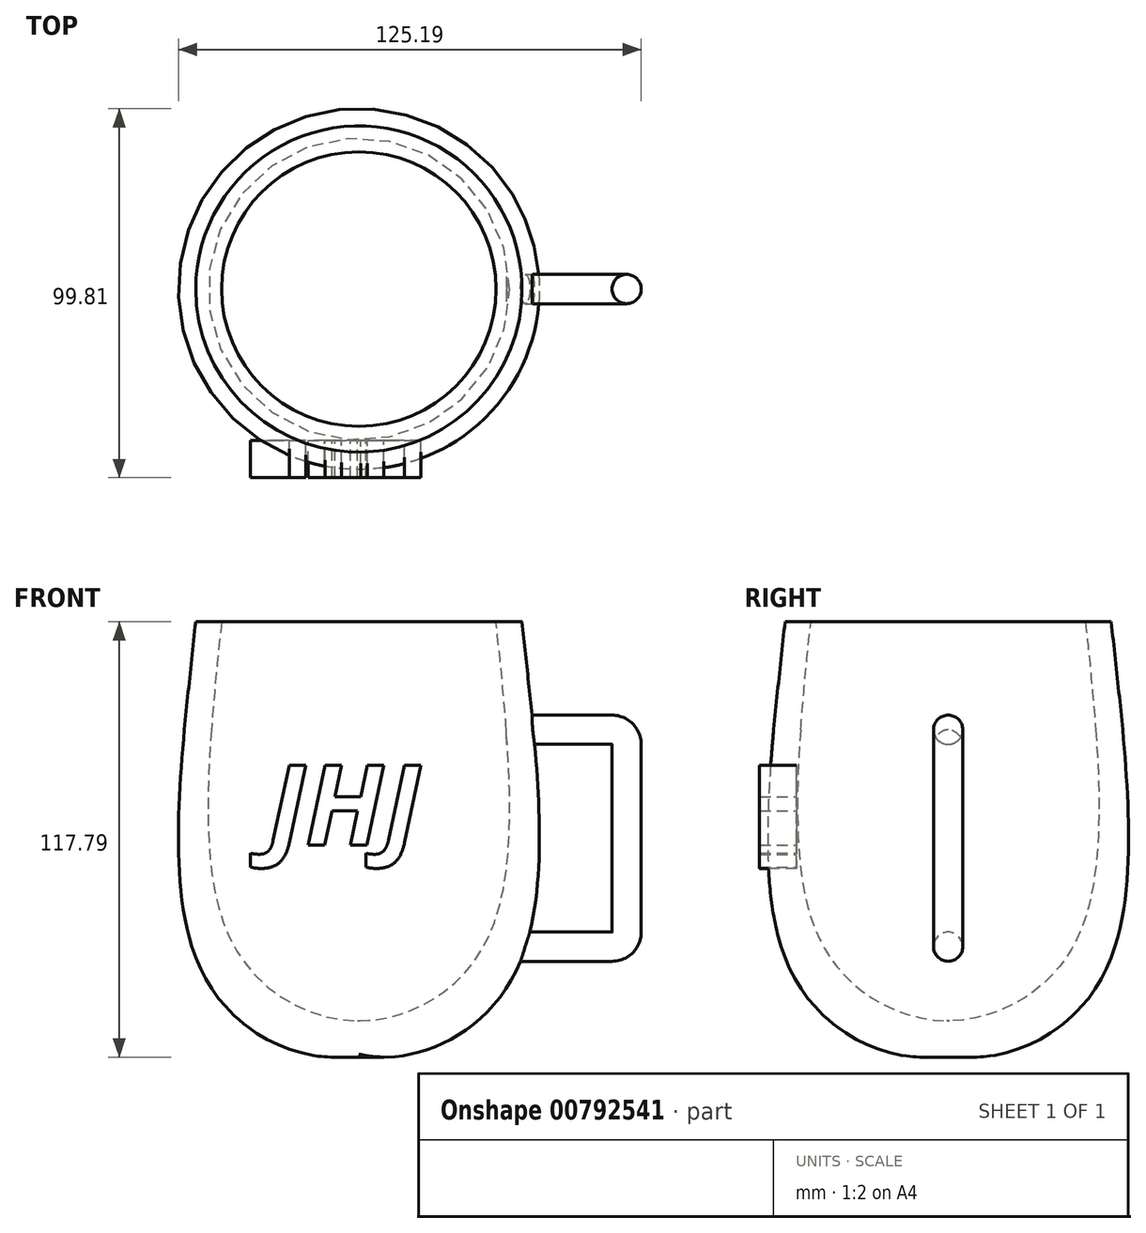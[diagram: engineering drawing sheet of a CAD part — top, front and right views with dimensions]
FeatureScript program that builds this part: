
annotation { "Feature Type Name" : "Feature", "Feature Type Description" : "" }
export const myFeature = defineFeature(function(context is Context, id is Id, definition is map)
    precondition{}
    {
        {
            var Q0;
            Q0=qCreatedBy(makeId("Front.planeOp"),FACE);
            var sketch = newSketch(context, id + "F0", { "sketchPlane" : qUnion([Q0])});
            skFitSpline(sketch, "E0", {"points": [v(0, -61.73) * mm, v(36.41, -35.88) * mm, v(35.16, 93.65) * mm], "startDerivative": vector(97.28, -1.16) * mm, "endDerivative": vector(18.9, 148.96) * mm});
            skFitSpline(sketch, "E1", {"points": [v(0, -70.74) * mm, v(43.6, -45.95) * mm, v(42.98, 94.18) * mm], "startDerivative": vector(109.3, -28.64) * mm, "endDerivative": vector(27.71, 172.05) * mm});
            skLineSegment(sketch, "E2", {"start": v(37.13, 46.22) * mm, "end": v(44.12, 46.22) * mm});
            skLineSegment(sketch, "E3", {"start": v(39.9, 16.99) * mm, "end": v(68.42, 16.99) * mm});
            skLineSegment(sketch, "E4", {"start": v(72.42, 12.99) * mm, "end": v(72.42, -37.71) * mm});
            skLineSegment(sketch, "E5", {"start": v(68.42, -41.71) * mm, "end": v(36.41, -41.71) * mm});
            skPoint(sketch, "E6.visualSharp", {"position": v(72.42, 16.99) * mm});
            skArc(sketch, "E6.filletArc", {"start": v(72.42, 12.99) * mm, "mid": v(71.25, 15.81) * mm, "end": v(68.42, 16.99) * mm});
            skPoint(sketch, "E7.visualSharp", {"position": v(72.42, -41.71) * mm});
            skArc(sketch, "E7.filletArc", {"start": v(68.42, -41.71) * mm, "mid": v(71.25, -40.54) * mm, "end": v(72.42, -37.71) * mm});
            skLineSegment(sketch, "E8", {"start": v(0, -70.74) * mm, "end": v(0, 56.7) * mm});
            skSolve(sketch);
        }
        {
            var Q0;
            {var subQ0=sQuery(id+"F0.wireOp",EDGE,"E2");Q0=makeQuery(id+"F0.imprint","IMPRINT",FACE,{"disambiguationData":[TD([[makeQuery(id+"F0.imprint","IMPRINT",EDGE,{"derivedFrom":subQ0}),-1.0]])]});}
            var Q1;
            {var subQ0=sQuery(id+"F0.wireOp",EDGE,"E5");var subQ1=sQuery(id+"F0.wireOp",EDGE,"E0");var subQ2=makeQuery(id+"F0.imprint","INTERSECT",VERTEX,{"derivedFrom":[subQ1,subQ0]});Q1=makeQuery(id+"F0.imprint","IMPRINT",FACE,{"disambiguationData":[TD([[makeQuery(id+"F0.imprint","IMPRINT",EDGE,{"disambiguationData":[TD([[subQ2,-1.0]])],"derivedFrom":subQ1}),-1.0]])]});}
            var Q2;
            {var subQ0=sQuery(id+"F0.wireOp",EDGE,"E8");var subQ1=sQuery(id+"F0.wireOp",EDGE,"E0");var subQ2=makeQuery(id+"F0.imprint","INTERSECT",VERTEX,{"derivedFrom":[subQ1,subQ0]});Q2=makeQuery(id+"F0.imprint","IMPRINT",FACE,{"disambiguationData":[TD([[makeQuery(id+"F0.imprint","IMPRINT",EDGE,{"disambiguationData":[TD([[subQ2,-1.0]])],"derivedFrom":subQ1}),-1.0]])]});}
            var Q3;
            Q3=sQuery(id+"F0.wireOp",EDGE,"E8");
            revolve(context, id + "F1", {"surfaceOperationType" : NewSurfaceOperationType.NEW, "entities" : qUnion([Q0, Q1, Q2]), "axis" : qUnion([Q3]), "revolveType" : RevolveType.FULL});
        }
        {
            var Q0;
            Q0=sQuery(id+"F0.wireOp",VERTEX,"E3.start");
            var Q1;
            Q1=sQuery(id+"F0.wireOp",EDGE,"E3");
            cPlane(context, id + "F2", {"entities" : qUnion([Q0, Q1]), "cplaneType" : CPlaneType.LINE_POINT, "offset" : 25 * mm, "width" : 150 * mm, "height" : 150 * mm});
        }
        {
            var Q0;
            Q0=qCreatedBy(id+"F2.planeOp",FACE);
            var sketch = newSketch(context, id + "F3", { "sketchPlane" : qUnion([Q0])});
            skCircle(sketch, "E9", {"center": v(0, -41.71) * mm, "radius": 3.95 * mm});
            skSolve(sketch);
        }
        {
            var Q0;
            Q0=makeQuery(id+"F3.imprint","IMPRINT",FACE,{"disambiguationData":[TD([[makeQuery(id+"F3.imprint","IMPRINT",EDGE,{"derivedFrom":sQuery(id+"F3.wireOp",EDGE,"E9")}),1.0]])]});
            var Q1;
            Q1=sQuery(id+"F0.wireOp",EDGE,"E5");
            var Q2;
            Q2=sQuery(id+"F0.wireOp",EDGE,"E7.filletArc");
            var Q3;
            Q3=sQuery(id+"F0.wireOp",EDGE,"E4");
            var Q4;
            Q4=sQuery(id+"F0.wireOp",EDGE,"E6.filletArc");
            var Q5;
            Q5=sQuery(id+"F0.wireOp",EDGE,"E3");
            sweep(context, id + "F4", {"operationType" : NewBodyOperationType.ADD, "profiles" : qUnion([Q0]), "path" : qUnion([Q1, Q2, Q3, Q4, Q5])});
        }
        {
            var Q0;
            Q0=qCreatedBy(makeId("Front.planeOp"),FACE);
            cPlane(context, id + "F5", {"entities" : qUnion([Q0]), "cplaneType" : CPlaneType.OFFSET, "offset" : 41 * mm, "width" : 150 * mm, "height" : 150 * mm});
        }
        {
            var Q0;
            Q0=qCreatedBy(id+"F5.planeOp",FACE);
            var sketch = newSketch(context, id + "F6", { "sketchPlane" : qUnion([Q0])});
            skText(sketch, "E10", { "text": "JHJ", "fontName": "OpenSans-BoldItalic.ttf"});
            const initialGuessF6  = {"E10": [-0.02453, -0.0142, 1, 0, 0.02175]};
            skSetInitialGuess(sketch, initialGuessF6);
            skSolve(sketch);
        }
        {
            var Q0;
            Q0 = qSketchRegion(id + "F6", true);
            extrude(context, id + "F7", {"entities" : qUnion([Q0]), "depth" : 10 * mm, "offsetDistance" : 25 * mm});
        }
    });
